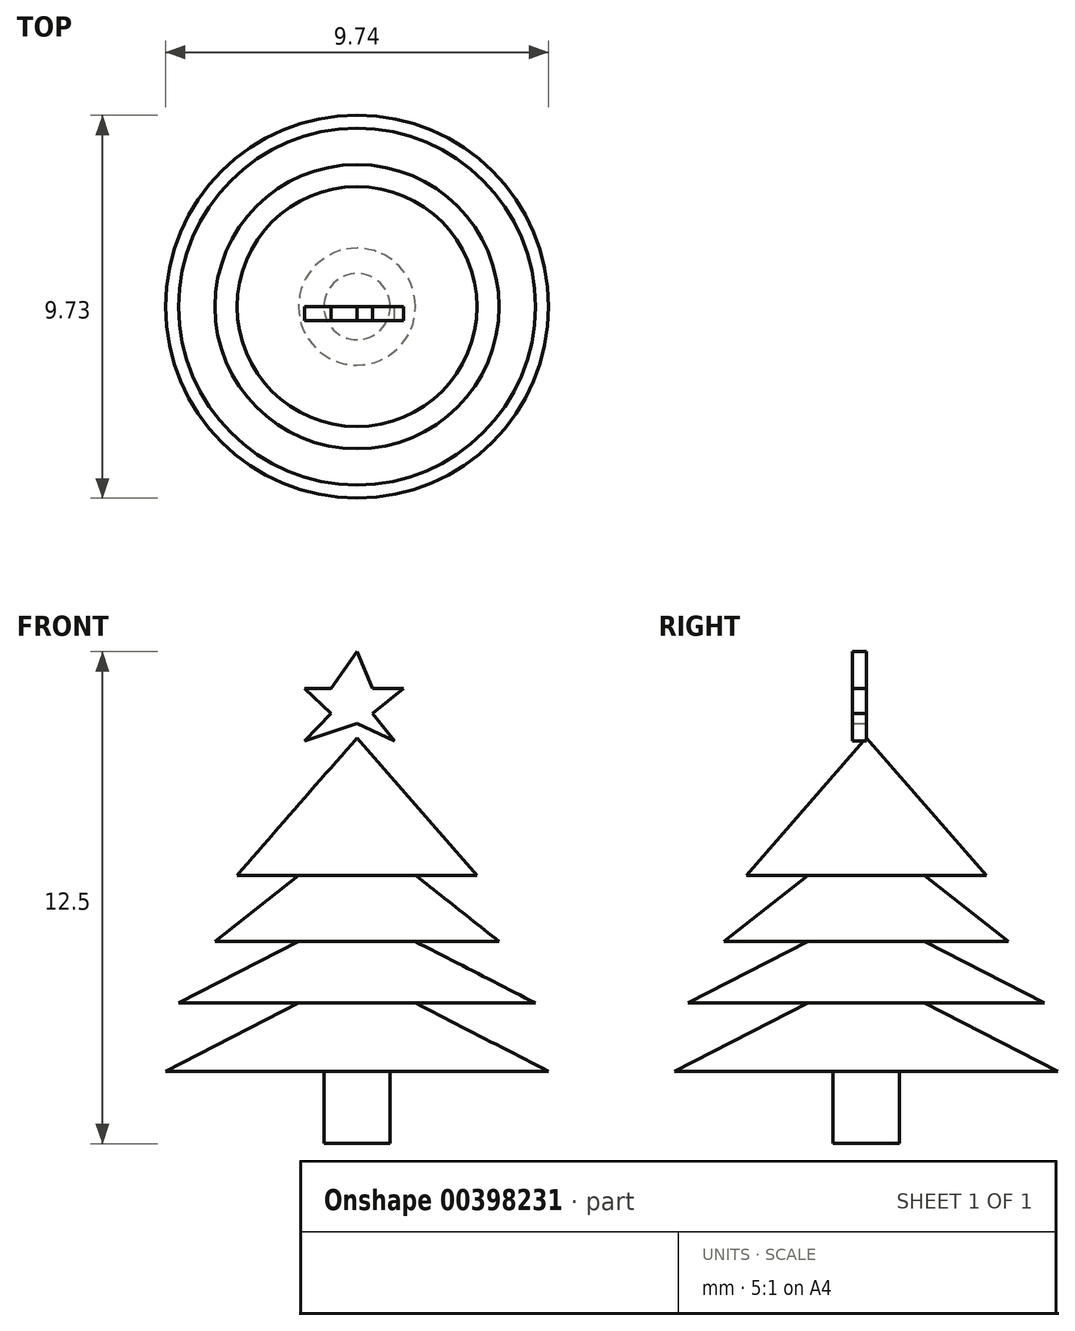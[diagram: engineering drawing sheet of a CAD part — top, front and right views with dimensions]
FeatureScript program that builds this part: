
annotation { "Feature Type Name" : "Feature", "Feature Type Description" : "" }
export const myFeature = defineFeature(function(context is Context, id is Id, definition is map)
    precondition{}
    {
        {
            var Q0;
            Q0=qCreatedBy(makeId("Front.planeOp"),FACE);
            var sketch = newSketch(context, id + "F0", { "sketchPlane" : qUnion([Q0])});
            skLineSegment(sketch, "E0", {"start": v(0, 39.3) * mm, "end": v(-17.78, 18.95) * mm});
            skPoint(sketch, "E1.end.orphan", {"position": v(0, 18.95) * mm});
            skLineSegment(sketch, "E2", {"start": v(-17.78, 18.95) * mm, "end": v(-8.66, 18.95) * mm});
            skLineSegment(sketch, "E3", {"start": v(-8.66, 18.95) * mm, "end": v(-21.06, 9.12) * mm});
            skLineSegment(sketch, "E4", {"start": v(-21.06, 9.12) * mm, "end": v(-8.66, 9.12) * mm});
            skLineSegment(sketch, "E5", {"start": v(-8.66, 9.12) * mm, "end": v(-26.44, 0) * mm});
            skLineSegment(sketch, "E6", {"start": v(-26.44, 0) * mm, "end": v(-8.66, 0) * mm});
            skLineSegment(sketch, "E7", {"start": v(-8.66, 0) * mm, "end": v(-28.38, -10.12) * mm});
            skLineSegment(sketch, "E8", {"start": v(-28.38, -10.12) * mm, "end": v(-4.91, -10.12) * mm});
            skLineSegment(sketch, "E9", {"start": v(-4.91, -10.12) * mm, "end": v(-4.91, -20.82) * mm});
            skLineSegment(sketch, "E10", {"start": v(-4.91, -20.82) * mm, "end": v(0, -20.82) * mm});
            skLineSegment(sketch, "E11", {"start": v(0, 39.3) * mm, "end": v(0, -20.82) * mm});
            skSolve(sketch);
        }
        {
            var Q0;
            Q0 = qSketchRegion(id + "F0", true);
            var Q1;
            Q1=sQuery(id+"F0.wireOp",EDGE,"E11");
            revolve(context, id + "F1", {"entities" : qUnion([Q0]), "axis" : qUnion([Q1]), "revolveType" : RevolveType.FULL});
        }
        {
            var Q0;
            Q0=qCreatedBy(makeId("Front.planeOp"),FACE);
            var sketch = newSketch(context, id + "F2", { "sketchPlane" : qUnion([Q0])});
            skLineSegment(sketch, "E12", {"start": v(-7.77, 38.85) * mm, "end": v(-3.89, 42.88) * mm});
            skPoint(sketch, "E12.endSnap0", {"position": v(-3.89, 38.85) * mm});
            skLineSegment(sketch, "E13", {"start": v(-3.89, 42.88) * mm, "end": v(-7.77, 46.63) * mm});
            skLineSegment(sketch, "E14", {"start": v(0, 52.1) * mm, "end": v(2.3, 46.63) * mm});
            skLineSegment(sketch, "E15", {"start": v(2.3, 46.63) * mm, "end": v(6.9, 46.63) * mm});
            skLineSegment(sketch, "E16", {"start": v(6.9, 46.63) * mm, "end": v(2.3, 42.88) * mm});
            skLineSegment(sketch, "E17", {"start": v(2.3, 42.88) * mm, "end": v(5.58, 38.85) * mm});
            skPoint(sketch, "E18.end.orphan", {"position": v(0, 38.85) * mm});
            skLineSegment(sketch, "E19", {"start": v(-7.77, 38.85) * mm, "end": v(0, 41.44) * mm});
            skLineSegment(sketch, "E20", {"start": v(0, 41.44) * mm, "end": v(5.58, 38.85) * mm});
            skPoint(sketch, "E21.end.orphan", {"position": v(-3.89, 46.63) * mm});
            skLineSegment(sketch, "E22", {"start": v(-7.77, 46.63) * mm, "end": v(-3.89, 46.63) * mm});
            skPoint(sketch, "E23.orphan", {"position": v(0, 46.63) * mm});
            skLineSegment(sketch, "E24", {"start": v(-3.89, 46.63) * mm, "end": v(0, 52.1) * mm});
            skSolve(sketch);
        }
        {
            var Q0;
            Q0=makeQuery(id+"F2.imprint","IMPRINT",FACE,{"disambiguationData":[TD([[makeQuery(id+"F2.imprint","IMPRINT",EDGE,{"derivedFrom":sQuery(id+"F2.wireOp",EDGE,"E12")}),-1.0]])]});
            extrude(context, id + "F3", {"entities" : qUnion([Q0]), "depth" : 2.03 * mm});
        }
        {
            var Q0;
            Q0=makeQuery(id+"F1.opRevolve","SWEPT_BODY",BODY,{"disambiguationData":[OSD([sQuery(id+"F0.wireOp",EDGE,"E0"),sQuery(id+"F0.wireOp",EDGE,"E2"),sQuery(id+"F0.wireOp",EDGE,"E3"),sQuery(id+"F0.wireOp",EDGE,"E4"),sQuery(id+"F0.wireOp",EDGE,"E5"),sQuery(id+"F0.wireOp",EDGE,"E6"),sQuery(id+"F0.wireOp",EDGE,"E7"),sQuery(id+"F0.wireOp",EDGE,"E8"),sQuery(id+"F0.wireOp",EDGE,"E9"),sQuery(id+"F0.wireOp",EDGE,"E10"),sQuery(id+"F0.wireOp",EDGE,"E11")])]});
            var Q1;
            Q1=makeQuery(id+"F3.opExtrude","SWEPT_BODY",BODY,{"disambiguationData":[OSD([sQuery(id+"F2.wireOp",EDGE,"E12"),sQuery(id+"F2.wireOp",EDGE,"E13"),sQuery(id+"F2.wireOp",EDGE,"E14"),sQuery(id+"F2.wireOp",EDGE,"E15"),sQuery(id+"F2.wireOp",EDGE,"E16"),sQuery(id+"F2.wireOp",EDGE,"E17"),sQuery(id+"F2.wireOp",EDGE,"E19"),sQuery(id+"F2.wireOp",EDGE,"E20"),sQuery(id+"F2.wireOp",EDGE,"E22"),sQuery(id+"F2.wireOp",EDGE,"E24")])]});
            var Q2;
            Q2=makeQuery(id+"F3.opExtrude","CAP_VERTEX",VERTEX,{"disambiguationData":[OSD([sQuery(id+"F2.wireOp",EDGE,"E14"),sQuery(id+"F2.wireOp",EDGE,"E24")])],"isStart":false});
            transform(context, id + "F4", {"entities" : qUnion([Q0, Q1]), "transformType" : TransformType.SCALE_UNIFORMLY, "scale" : 1.2 / 7, "scalePoint" : qUnion([Q2]), "makeCopy" : false});
        }
    });
